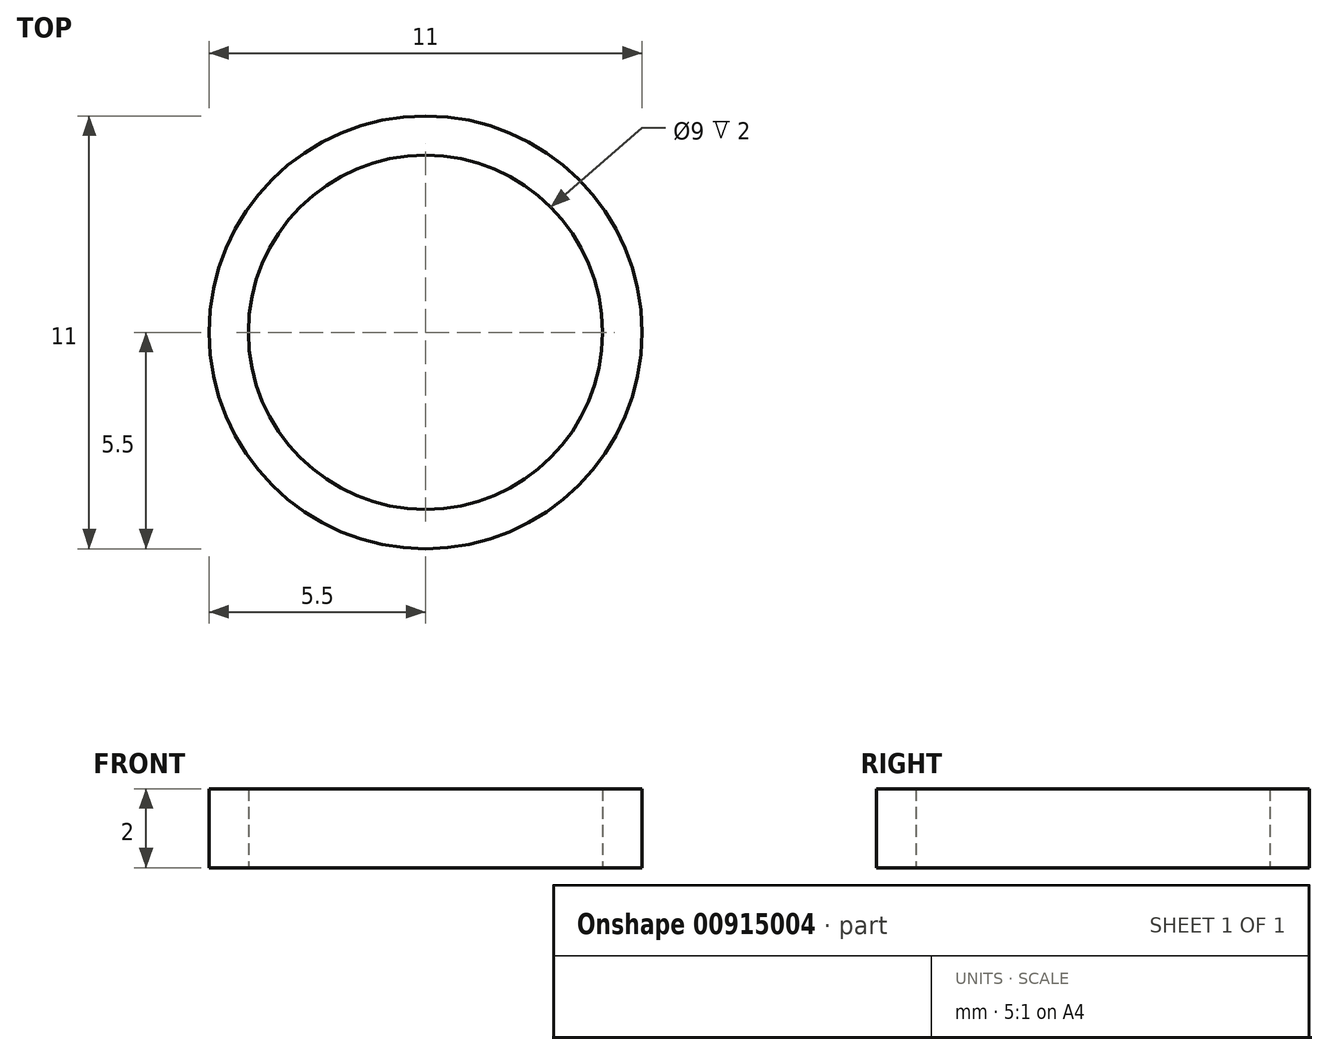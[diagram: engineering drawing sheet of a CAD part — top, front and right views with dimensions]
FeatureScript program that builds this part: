
annotation { "Feature Type Name" : "Feature", "Feature Type Description" : "" }
export const myFeature = defineFeature(function(context is Context, id is Id, definition is map)
    precondition{}
    {
        {
            var Q0;
            Q0=qCreatedBy(makeId("Top.planeOp"),FACE);
            var sketch = newSketch(context, id + "F0", { "sketchPlane" : qUnion([Q0])});
            skCircle(sketch, "E0", {"center": v(0, 0) * mm, "radius": 5.5 * mm});
            skCircle(sketch, "E1", {"center": v(0, 0) * mm, "radius": 4.5 * mm});
            skSolve(sketch);
        }
        {
            var Q0;
            Q0=makeQuery(id+"F0.imprint","IMPRINT",FACE,{"disambiguationData":[TD([[makeQuery(id+"F0.imprint","IMPRINT",EDGE,{"derivedFrom":sQuery(id+"F0.wireOp",EDGE,"E0")}),1.0]])]});
            extrude(context, id + "F1", {"entities" : qUnion([Q0]), "depth" : 2 * mm, "offsetDistance" : 25.4 * mm});
        }
    });
